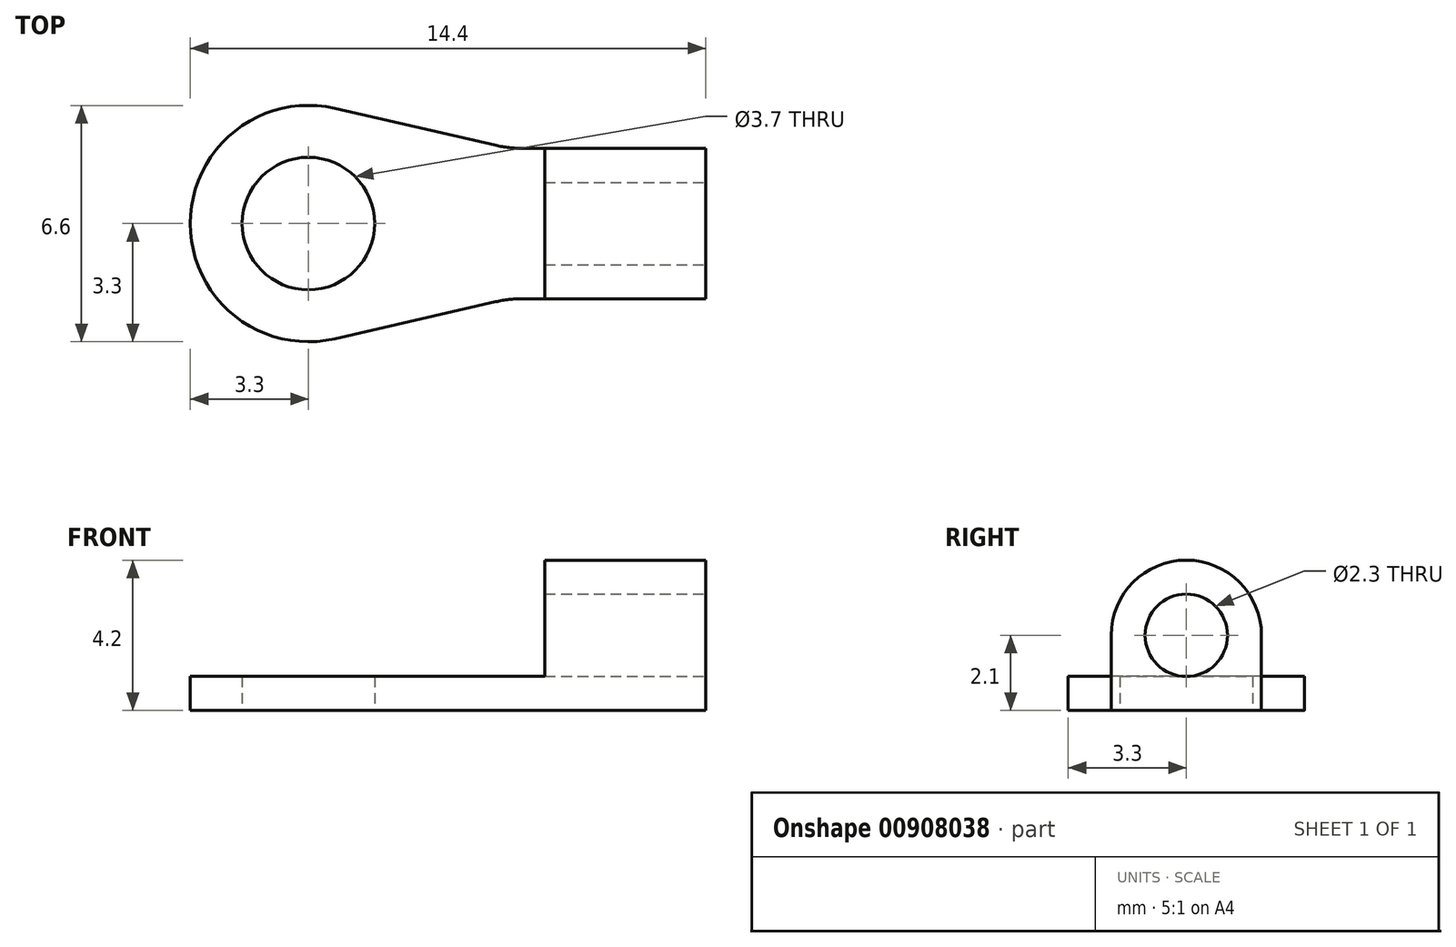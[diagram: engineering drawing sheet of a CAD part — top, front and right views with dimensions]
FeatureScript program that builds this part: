
annotation { "Feature Type Name" : "Feature", "Feature Type Description" : "" }
export const myFeature = defineFeature(function(context is Context, id is Id, definition is map)
    precondition{}
    {
        {
            var Q0;
            Q0=qCreatedBy(makeId("Top.planeOp"),FACE);
            var sketch = newSketch(context, id + "F0", { "sketchPlane" : qUnion([Q0])});
            skLineSegment(sketch, "E0.left", {"start": v(0, 3.3) * mm, "end": v(0, 3.3) * mm});
            skLineSegment(sketch, "E0.right", {"start": v(14.4, 1.2) * mm, "end": v(14.4, 5.4) * mm});
            skPoint(sketch, "E1.visualSharp", {"position": v(0, 6.6) * mm});
            skArc(sketch, "E1.filletArc", {"start": v(3.3, 6.6) * mm, "mid": v(0.97, 5.63) * mm, "end": v(0, 3.3) * mm});
            skPoint(sketch, "E2.visualSharp", {"position": v(0, 0) * mm});
            skArc(sketch, "E2.filletArc", {"start": v(0, 3.3) * mm, "mid": v(0.97, 0.97) * mm, "end": v(3.3, 0) * mm});
            skLineSegment(sketch, "E3.bottom", {"start": v(14.4, 1.2) * mm, "end": v(9.27, 1.2) * mm});
            skLineSegment(sketch, "E3.top", {"start": v(14.4, 5.4) * mm, "end": v(9.27, 5.4) * mm});
            skPoint(sketch, "E3.middle", {"position": v(14.4, 3.3) * mm});
            skArc(sketch, "E4", {"start": v(4.04, 6.52) * mm, "mid": v(0, 3.3) * mm, "end": v(4.04, 0.08) * mm});
            skCircle(sketch, "E5", {"center": v(3.3, 3.3) * mm, "radius": 1.85 * mm});
            skLineSegment(sketch, "E6", {"start": v(8.54, 5.48) * mm, "end": v(4.04, 6.52) * mm});
            skLineSegment(sketch, "E7", {"start": v(8.54, 1.12) * mm, "end": v(4.04, 0.08) * mm});
            skPoint(sketch, "E8.orphan", {"position": v(18.9, 5.4) * mm});
            skPoint(sketch, "E9.orphan", {"position": v(18.9, 1.2) * mm});
            skPoint(sketch, "E0.bottom.end.orphan", {"position": v(14.4, 0) * mm});
            skPoint(sketch, "E0.top.end.orphan", {"position": v(14.4, 6.6) * mm});
            skPoint(sketch, "E3.right.end.orphan", {"position": v(9.9, 5.4) * mm});
            skPoint(sketch, "E3.right.start.orphan", {"position": v(9.9, 1.2) * mm});
            skPoint(sketch, "E10.visualSharp", {"position": v(8.9, 5.4) * mm});
            skArc(sketch, "E10.filletArc", {"start": v(8.54, 5.48) * mm, "mid": v(8.9, 5.42) * mm, "end": v(9.27, 5.4) * mm});
            skPoint(sketch, "E11.visualSharp", {"position": v(8.9, 1.2) * mm});
            skArc(sketch, "E11.filletArc", {"start": v(9.27, 1.2) * mm, "mid": v(8.9, 1.18) * mm, "end": v(8.54, 1.12) * mm});
            skSolve(sketch);
        }
        {
            var Q0;
            Q0=makeQuery(id+"F0.imprint","IMPRINT",FACE,{"disambiguationData":[TD([[makeQuery(id+"F0.imprint","IMPRINT",EDGE,{"derivedFrom":sQuery(id+"F0.wireOp",EDGE,"E0.right")}),1.0]])]});
            extrude(context, id + "F1", {"entities" : qUnion([Q0]), "depth" : 0.95 * mm, "offsetDistance" : 25 * mm});
        }
        {
            var Q0;
            Q0=makeQuery(id+"F1.opExtrude","CAP_FACE",FACE,{"disambiguationData":[OSD([sQuery(id+"F0.wireOp",EDGE,"E0.right"),sQuery(id+"F0.wireOp",EDGE,"E3.bottom"),sQuery(id+"F0.wireOp",EDGE,"E3.top"),sQuery(id+"F0.wireOp",EDGE,"E4"),sQuery(id+"F0.wireOp",EDGE,"E5"),sQuery(id+"F0.wireOp",EDGE,"E6"),sQuery(id+"F0.wireOp",EDGE,"E7"),sQuery(id+"F0.wireOp",EDGE,"E10.filletArc"),sQuery(id+"F0.wireOp",EDGE,"E11.filletArc")])],"isStart":false});
            var sketch = newSketch(context, id + "F2", { "sketchPlane" : qUnion([Q0])});
            skLineSegment(sketch, "E12.bottom", {"start": v(14.4, 5.4) * mm, "end": v(9.9, 5.4) * mm});
            skLineSegment(sketch, "E12.top", {"start": v(14.4, 1.2) * mm, "end": v(9.9, 1.2) * mm});
            skLineSegment(sketch, "E12.left", {"start": v(14.4, 5.4) * mm, "end": v(14.4, 1.2) * mm});
            skLineSegment(sketch, "E12.right", {"start": v(9.9, 5.4) * mm, "end": v(9.9, 1.2) * mm});
            skSolve(sketch);
        }
        {
            var Q0;
            Q0=makeQuery(id+"F2.imprint","IMPRINT",FACE,{"disambiguationData":[TD([[makeQuery(id+"F2.imprint","IMPRINT",EDGE,{"derivedFrom":sQuery(id+"F2.wireOp",EDGE,"E12.bottom")}),1.0]])]});
            extrude(context, id + "F3", {"entities" : qUnion([Q0]), "operationType" : NewBodyOperationType.ADD, "depth" : 3.25 * mm, "offsetDistance" : 25 * mm});
        }
        {
            var Q0;
            Q0=makeQuery(id+"F3.opExtrude","CAP_EDGE",EDGE,{"disambiguationData":[OSD([sQuery(id+"F2.wireOp",EDGE,"E12.bottom")])],"isStart":false});
            var Q1;
            Q1=makeQuery(id+"F3.opExtrude","CAP_EDGE",EDGE,{"disambiguationData":[OSD([sQuery(id+"F2.wireOp",EDGE,"E12.top")])],"isStart":false});
            fillet(context, id + "F4", {"entities" : qUnion([Q0, Q1]), "radius" : 2.1 * mm, "tangentPropagation" : true, "allowEdgeOverflow" : false});
        }
        {
            var Q0;
            Q0=makeQuery(id+"F3.boolean.opBoolean","MERGE",FACE,{"derivedFrom":[makeQuery(id+"F1.opExtrude","SWEPT_FACE",FACE,{"disambiguationData":[OSD([sQuery(id+"F0.wireOp",EDGE,"E0.right")])]}),makeQuery(id+"F3.opExtrude","SWEPT_FACE",FACE,{"disambiguationData":[OSD([sQuery(id+"F2.wireOp",EDGE,"E12.left")])]})]});
            var sketch = newSketch(context, id + "F5", { "sketchPlane" : qUnion([Q0])});
            skCircle(sketch, "E13", {"center": v(3.3, 2.1) * mm, "radius": 1.15 * mm});
            skSolve(sketch);
        }
        {
            var Q0;
            Q0=makeQuery(id+"F5.imprint","IMPRINT",FACE,{"disambiguationData":[TD([[makeQuery(id+"F5.imprint","IMPRINT",EDGE,{"derivedFrom":sQuery(id+"F5.wireOp",EDGE,"E13")}),1.0]])]});
            extrude(context, id + "F6", {"entities" : qUnion([Q0]), "operationType" : NewBodyOperationType.REMOVE, "oppositeDirection" : true, "depth" : 25 * mm, "offsetDistance" : 25 * mm});
        }
    });
